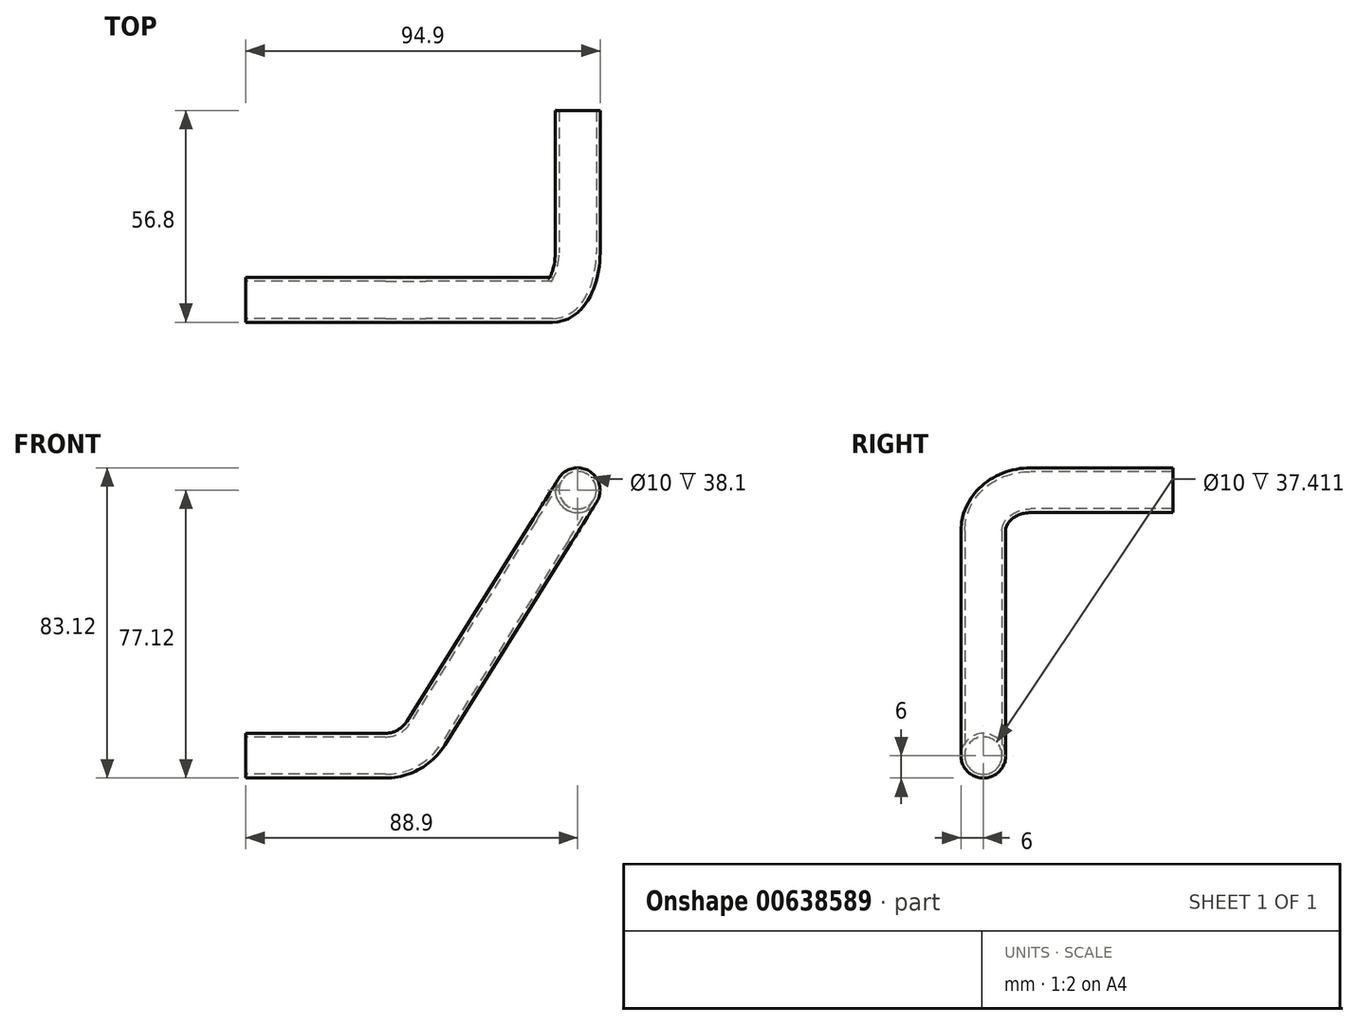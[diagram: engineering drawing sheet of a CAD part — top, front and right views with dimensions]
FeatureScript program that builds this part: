
annotation { "Feature Type Name" : "Feature", "Feature Type Description" : "" }
export const myFeature = defineFeature(function(context is Context, id is Id, definition is map)
    precondition{}
    {
        {
            var Q0;
            Q0=qCreatedBy(makeId("Front.planeOp"),FACE);
            var sketch = newSketch(context, id + "F0", { "sketchPlane" : qUnion([Q0])});
            skCircle(sketch, "E0", {"center": v(0, 0) * mm, "radius": 5 * mm});
            skCircle(sketch, "E1", {"center": v(0, 0) * mm, "radius": 6 * mm});
            skSolve(sketch);
        }
        {
            var Q0;
            Q0=qCreatedBy(makeId("Top.planeOp"),FACE);
            var sketch = newSketch(context, id + "F1", { "sketchPlane" : qUnion([Q0])});
            skLineSegment(sketch, "E2", {"start": v(0, 0) * mm, "end": v(0, -50.8) * mm, "construction": true});
            skLineSegment(sketch, "E3", {"start": v(0, -50.8) * mm, "end": v(-88.9, -50.8) * mm, "construction": true});
            skSolve(sketch);
        }
        {
            var Q0;
            Q0=sQuery(id+"F1.wireOp",EDGE,"E3");
            cPlane(context, id + "F2", {"entities" : qUnion([Q0]), "cplaneType" : CPlaneType.LINE_ANGLE, "offset" : 25.4 * mm, "angle" : 0 * degree, "width" : 152.4 * mm, "height" : 152.4 * mm});
        }
        {
            var Q0;
            Q0=qCreatedBy(id+"F2.planeOp",FACE);
            var sketch = newSketch(context, id + "F3", { "sketchPlane" : qUnion([Q0])});
            skLineSegment(sketch, "E4", {"start": v(-88.9, 0) * mm, "end": v(-88.9, -71.12) * mm, "construction": true});
            skPoint(sketch, "E5.0", {"position": v(-88.9, 0) * mm});
            skPoint(sketch, "E6.0", {"position": v(-44.45, 0) * mm});
            skPoint(sketch, "E7.0", {"position": v(0, 0) * mm});
            skLineSegment(sketch, "E8", {"start": v(-88.9, -71.12) * mm, "end": v(-51.49, -71.12) * mm});
            skLineSegment(sketch, "E9", {"start": v(-40.72, -65.15) * mm, "end": v(0, 0) * mm, "construction": true});
            skPoint(sketch, "E10.visualSharp", {"position": v(-44.45, -71.12) * mm});
            skArc(sketch, "E10.filletArc", {"start": v(-51.49, -71.12) * mm, "mid": v(-45.33, -69.53) * mm, "end": v(-40.72, -65.15) * mm});
            skSolve(sketch);
        }
        {
            var Q0;
            Q0=sQuery(id+"F3.wireOp",EDGE,"E9");
            cPlane(context, id + "F4", {"entities" : qUnion([Q0]), "cplaneType" : CPlaneType.LINE_ANGLE, "offset" : 25.4 * mm, "angle" : 0 * degree, "width" : 152.4 * mm, "height" : 152.4 * mm});
        }
        {
            var Q0;
            Q0=qCreatedBy(id+"F4.planeOp",FACE);
            var sketch = newSketch(context, id + "F5", { "sketchPlane" : qUnion([Q0])});
            skPoint(sketch, "E11.0", {"position": v(0, 0) * mm});
            skPoint(sketch, "E12.0", {"position": v(-50.8, 0) * mm});
            skPoint(sketch, "E13.0", {"position": v(-50.8, -76.83) * mm});
            skLineSegment(sketch, "E14", {"start": v(-50.8, -76.83) * mm, "end": v(-50.8, -12.7) * mm});
            skLineSegment(sketch, "E15", {"start": v(-38.1, 0) * mm, "end": v(0, 0) * mm});
            skArc(sketch, "E16.filletArc", {"start": v(-38.1, 0) * mm, "mid": v(-47.08, -3.72) * mm, "end": v(-50.8, -12.7) * mm});
            skSolve(sketch);
        }
        {
            var Q0;
            Q0=makeQuery(id+"F0.imprint","IMPRINT",FACE,{"disambiguationData":[TD([[makeQuery(id+"F0.imprint","IMPRINT",EDGE,{"derivedFrom":sQuery(id+"F0.wireOp",EDGE,"E0")}),-1.0]])]});
            var Q1;
            Q1=sQuery(id+"F5.wireOp",EDGE,"E15");
            var Q2;
            Q2=sQuery(id+"F5.wireOp",EDGE,"E16.filletArc");
            var Q3;
            Q3=sQuery(id+"F5.wireOp",EDGE,"E14");
            var Q4;
            Q4=sQuery(id+"F3.wireOp",EDGE,"E10.filletArc");
            var Q5;
            Q5=sQuery(id+"F3.wireOp",EDGE,"E8");
            sweep(context, id + "F6", {"profiles" : qUnion([Q0]), "path" : qUnion([Q1, Q2, Q3, Q4, Q5])});
        }
    });
